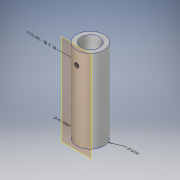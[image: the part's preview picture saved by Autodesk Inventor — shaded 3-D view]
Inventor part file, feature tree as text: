
AUTODESK INVENTOR PART (.ipt)
format: ipt  version: 2018.3 (Build 223284000, 284)  size: 131,072 bytes
history: native  units: in
note: dims shown in document units (in); Inventor stores cm internally (conversion verified against a paired STEP export)
features: hole x4, other x2, sketch x2, extrude x1, plane x1
ambient origin geometry x8: Origin, YZ Plane, XZ Plane, XY Plane, X Axis, Y Axis, Z Axis, Center Point
bodies: Solid1 (feature_tree)
feature tree (10):
  other  "Annotations"
  extrude  "Extrusion1"  Depth=1.0in
  hole  "Hole1"  [1 undecoded]
  plane  "Work Plane1"
  hole  "Hole2"  [1 undecoded]
  sketch  "Sketch1"  dims[d0=1.9in d1=0.0in d38=1.0in d39=1.0in]
  sketch  "Sketch2"  dims[d5=0.5in d6=0.119in d7=0.25in d8=0.5635in d9=1.9in d10=0.8108in d11=1.6in d12=0.104in d13=0.276in d14=0.375in d15=0.25in d16=0.5635in d17=0.4in d18=0.8108in d42=0.3in d23=0.0in d25=1.2359in d26=0.3358in d27=0.3804in d29=2.3209in d30=0.625in]
  hole  "Hole Note 1"  [1 undecoded]
  hole  "Hole Note 2"  [1 undecoded]
  other  "Diameter Dimension 1"
note: 4 required parameter values undecoded (feature->parameter linkage not recoverable at this tier; creation-order binding heuristic only, values carry confidence <= 0.55)
